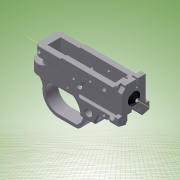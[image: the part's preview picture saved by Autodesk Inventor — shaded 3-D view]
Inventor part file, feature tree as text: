
AUTODESK INVENTOR PART (.ipt)
format: ipt  version: 2011 (Build 150239000, 239)  size: 1,561,600 bytes
history: native  units: in
note: dims shown in document units (in); Inventor stores cm internally (conversion verified against a paired STEP export)
features: sketch x72, extrude x66, fillet x50, projected_geometry x7, hole x5, reference x5, other x1, plane x1, revolve x1
ambient origin geometry x8: Origin, YZ Plane, XZ Plane, XY Plane, X Axis, Y Axis, Z Axis, Center Point
bodies: Solid1 (feature_tree)
feature tree (208):
  extrude  "Extrusion1"  Depth=3.698in
  hole  "Hole1"  [1 undecoded]
  extrude  "Extrusion2"  Depth=0.235in
  sketch  "Sketch4"  dims[d16=0.235in d17=0.235in]
  extrude  "Extrusion3"  Depth=2.655in
  extrude  "Extrusion4"  Depth=0.778in
  extrude  "Extrusion5"  Depth=1.0in TaperAngle=0.0deg
  extrude  "Extrusion6"  Depth=1.244in TaperAngle=0.0deg
  extrude  "Extrusion7"  Depth=0.4805in
  extrude  "Extrusion8"  Depth=0.821in
  extrude  "Extrusion9"  Depth=1.244in TaperAngle=0.0deg
  extrude  "Extrusion10"  Depth=0.44in
  extrude  "Extrusion11"  Depth=0.174in
  extrude  "Extrusion12"  Depth=0.105in TaperAngle=0.0deg
  fillet  "Fillet2"  Radius=0.105in
  fillet  "Fillet3"  Radius=0.442in
  extrude  "Extrusion13"  Depth=0.092in TaperAngle=0.0deg
  extrude  "Extrusion14"  Depth=0.125in
  other  "Work Axis1"
  plane  "Work Plane1"
  revolve  "Revolution1"  [1 undecoded]
  extrude  "Extrusion15"  Depth=0.131in TaperAngle=0.0deg
  extrude  "Extrusion16"  TaperAngle=90.0deg  [1 undecoded]
  extrude  "Extrusion17"  Depth=0.1875in TaperAngle=0.0deg
  extrude  "Extrusion19"  Depth=0.44in
  extrude  "Extrusion20"  Depth=0.4805in
  extrude  "Extrusion21"  Depth=0.46in TaperAngle=0.0deg
  fillet  "Fillet4"  Radius=0.46in
  fillet  "Fillet5"  Radius=0.895in
  fillet  "Fillet6"  Radius=0.2375in
  fillet  "Fillet7"  Radius=0.46in
  fillet  "Fillet8"  Radius=0.0625in
  fillet  "Fillet9"  Radius=0.0625in
  fillet  "Fillet10"  Radius=0.0625in
  extrude  "Extrusion22"  Depth=0.0625in
  fillet  "Fillet11"  Radius=0.0625in
  fillet  "Fillet12"  Radius=0.0625in
  extrude  "Extrusion23"  Depth=0.0625in
  extrude  "Extrusion24"  Depth=0.46in TaperAngle=0.0deg
  fillet  "Fillet13"  Radius=1.125in
  extrude  "Extrusion25"  Depth=0.042in
  extrude  "Extrusion26"  Depth=0.042in TaperAngle=0.0deg
  fillet  "Fillet15"  Radius=0.042in
  extrude  "Extrusion27"  Depth=0.085in TaperAngle=0.0deg
  extrude  "Extrusion28"  Depth=0.085in TaperAngle=0.0deg
  extrude  "Extrusion29"  Depth=0.375in
  extrude  "Extrusion30"  Depth=0.1875in
  fillet  "Fillet16"  Radius=0.125in
  fillet  "Fillet17"  Radius=0.125in
  fillet  "Fillet18"  Radius=0.0312in
  fillet  "Fillet19"  Radius=0.0312in
  fillet  "Fillet20"  Radius=0.0312in
  fillet  "Fillet21"  Radius=0.0312in
  fillet  "Fillet22"  Radius=0.0312in
  fillet  "Fillet23"  Radius=0.0312in
  fillet  "Fillet24"  Radius=0.0312in
  fillet  "Fillet25"  Radius=0.0312in
  fillet  "Fillet26"  Radius=0.085in
  fillet  "Fillet27"  Radius=0.911in
  fillet  "Fillet28"  Radius=1.781in
  extrude  "Extrusion31"  Depth=0.6in
  extrude  "Extrusion32"  Depth=0.583in
  extrude  "Extrusion33"  Depth=0.125in
  extrude  "Extrusion34"  Depth=0.085in TaperAngle=0.0deg
  extrude  "Extrusion35"  Depth=0.125in TaperAngle=0.0deg
  fillet  "Fillet29"  Radius=0.0625in
  fillet  "Fillet30"  Radius=0.0625in
  fillet  "Fillet31"  Radius=0.0625in
  fillet  "Fillet32"  Radius=0.0625in
  fillet  "Fillet33"  Radius=0.0625in
  extrude  "Extrusion36"  Depth=1.471in
  hole  "Hole2"  [1 undecoded]
  extrude  "Extrusion37"  Depth=1.975in
  extrude  "Extrusion38"  Depth=0.3205in
  hole  "Hole3"  [1 undecoded]
  extrude  "Extrusion39"  Depth=1.977in
  extrude  "Extrusion40"  Depth=0.5in
  extrude  "Extrusion41"  Depth=0.266in
  fillet  "Fillet34"  Radius=1.125in
  fillet  "Fillet35"  Radius=1.765in
  extrude  "Extrusion42"  Depth=0.1875in
  fillet  "Fillet36"  Radius=1.25in
  extrude  "Extrusion43"  Depth=0.0625in
  extrude  "Extrusion44"  Depth=0.25in TaperAngle=0.0deg
  fillet  "Fillet37"  Radius=0.125in
  fillet  "Fillet38"  Radius=0.184in
  fillet  "Fillet39"  Radius=0.184in
  fillet  "Fillet40"  Radius=0.125in
  fillet  "Fillet41"  Radius=0.0312in
  fillet  "Fillet42"  Radius=0.0312in
  extrude  "Extrusion45"  Depth=0.0312in
  hole  "Hole4"  [1 undecoded]
  extrude  "Extrusion46"  Depth=0.326in
  extrude  "Extrusion47"  Depth=0.6in TaperAngle=0.0deg
  fillet  "Fillet43"  Radius=0.911in
  fillet  "Fillet44"  Radius=0.75in
  extrude  "Extrusion48"  Depth=0.6in TaperAngle=0.0deg
  extrude  "Extrusion49"  Depth=0.0312in
  extrude  "Extrusion50"  Depth=1.0in TaperAngle=0.0deg
  extrude  "Extrusion51"  Depth=1.0in TaperAngle=0.0deg
  fillet  "Fillet45"  Radius=0.1125in
  fillet  "Fillet46"  Radius=0.125in
  extrude  "Extrusion52"  Depth=0.1125in TaperAngle=0.0deg
  extrude  "Extrusion53"  Depth=0.1125in TaperAngle=0.0deg
  extrude  "Extrusion54"  Depth=0.1125in TaperAngle=0.0deg
  fillet  "Fillet47"  Radius=2.321in
  extrude  "Extrusion55"  Depth=1.721in
  hole  "Hole5"  [1 undecoded]
  extrude  "Extrusion56"  Depth=1.5in TaperAngle=0.0deg
  extrude  "Extrusion57"  Depth=1.5in TaperAngle=0.0deg
  extrude  "Extrusion58"  Depth=0.125in
  extrude  "Extrusion59"  Depth=1.5in TaperAngle=0.0deg
  extrude  "Extrusion60"  Depth=1.5in TaperAngle=0.0deg
  fillet  "Fillet48"  Radius=0.125in
  fillet  "Fillet49"  Radius=1.5in
  fillet  "Fillet50"  Radius=0.125in
  extrude  "Extrusion61"  Depth=1.5in TaperAngle=0.0deg
  extrude  "Extrusion62"  [1 undecoded]
  extrude  "Extrusion63"  [1 undecoded]
  fillet  "Fillet51"  [1 undecoded]
  extrude  "Extrusion64"  [1 undecoded]
  fillet  "Fillet52"  [1 undecoded]
  extrude  "Extrusion65"  [1 undecoded]
  extrude  "Extrusion66"  [1 undecoded]
  extrude  "Extrusion67"  [1 undecoded]
  sketch  "Sketch1"  dims[d0=1.0in d1=3.698in]
  sketch  "Sketch2"  dims[d2=0.97in d3=0.0in]
  sketch  "Sketch3"  dims[d5=0.1875in d6=0.5in d7=0.375in d8=0.25in d9=0.5635in d10=0.75in d11=0.8108in d12=0.198in d13=0.0in]
  sketch  "Sketch5"  dims[d18=0.65in d19=2.655in]
  sketch  "Sketch6"  dims[d20=3.596in d21=0.778in]
  sketch  "Sketch7"  dims[d22=3.886in d23=1.0in d24=0.0in]
  sketch  "Sketch8"  dims[d25=1.0in d26=0.0in d27=1.244in d28=0.0in]
  sketch  "Sketch9"  dims[d29=0.961in d30=0.4805in]
  sketch  "Sketch10"  dims[d31=0.821in d32=0.821in]
  sketch  "Sketch11"  dims[d33=1.244in d34=0.0in d35=1.244in d36=0.0in]
  sketch  "Sketch12"  dims[d37=1.244in d38=0.0in d39=0.44in]
  sketch  "Sketch13"  dims[d40=0.585in d41=0.174in]
  sketch  "Sketch14"  dims[d42=0.125in d43=0.105in d44=0.0in d45=0.105in d46=0.0in d47=0.442in]
  sketch  "Sketch15"  dims[d48=0.092in d49=0.0in d50=0.092in d51=0.0in]
  sketch  "Sketch16"  dims[d52=0.125in d53=0.125in]
  projected_geometry  "Projected Loop2"
  sketch  "Sketch17"  dims[d67=0.458in d68=0.0in d69=0.48in]
  sketch  "Sketch18"  dims[d70=0.148in d71=0.131in d72=0.0in]
  sketch  "Sketch19"  dims[d73=90.0deg d74=90.0deg]
  sketch  "Sketch21"  dims[d75=0.418in d76=0.1875in d77=0.0in]
  projected_geometry  "Projected Loop3"
  sketch  "Sketch22"  dims[d80=0.1875in d81=0.0in d82=0.44in]
  sketch  "Sketch23"  dims[d83=0.4805in d84=0.4805in]
  sketch  "Sketch24"  dims[d87=0.55in d88=0.0in d91=0.46in d92=0.0in d93=0.46in d94=0.0in d95=0.895in d96=0.2375in d97=0.2375in d98=0.46in d99=0.0in d100=0.0625in d101=0.0625in d102=0.0625in]
  sketch  "Sketch25"  dims[d103=0.0625in d104=0.0625in d105=0.0625in d106=0.0625in]
  sketch  "Sketch26"  dims[d107=0.46in d108=0.0in d109=0.0625in]
  sketch  "Sketch27"  dims[d110=0.0625in d111=0.46in d112=0.0in d113=1.125in]
  sketch  "Sketch28"  dims[d114=0.042in d115=0.0in d116=0.042in]
  sketch  "Sketch29"  dims[d118=1.769in d119=0.042in d120=0.0in d121=0.042in d122=0.0in]
  sketch  "Sketch30"  dims[d123=0.375in d124=0.085in d125=0.0in]
  sketch  "Sketch31"  dims[d126=0.085in d127=0.0in d128=0.085in d129=0.0in]
  sketch  "Sketch32"  dims[d130=0.085in d131=0.0in d132=0.375in]
  sketch  "Sketch33"  dims[d133=0.125in d134=0.1875in d135=0.125in d136=0.125in d137=0.0312in d138=0.0312in d139=0.0312in d140=0.0312in d141=0.0312in d142=0.0312in d143=0.0312in d144=0.0312in d147=0.085in d148=0.0in d149=0.911in d150=1.781in]
  sketch  "Sketch34"  dims[d152=0.085in d153=0.6in]
  sketch  "Sketch35"  dims[d156=1.1875in d157=0.583in]
  sketch  "Sketch36"  dims[d158=0.085in d159=0.0in d168=0.125in]
  sketch  "Sketch37"  dims[d174=0.125in d175=0.085in d176=0.0in]
  sketch  "Sketch38"  dims[d177=0.125in d178=0.0in d179=0.125in d180=0.0in d181=0.0625in d182=0.0625in d183=0.0625in d184=0.0625in d185=0.0625in]
  sketch  "Sketch39"  dims[d186=1.471in d187=1.471in]
  sketch  "Sketch40"  dims[d188=0.3125in d189=0.125in d190=0.0in]
  sketch  "Sketch41"  dims[d191=1.304in]
  projected_geometry  "Projected Loop4"
  sketch  "Sketch42"  dims[d192=0.125in d193=0.5in d194=0.375in d195=0.25in d196=0.5635in d197=0.75in d198=0.8108in d199=1.975in]
  sketch  "Sketch43"  dims[d200=0.3205in d201=0.3205in]
  projected_geometry  "Projected Loop5"
  sketch  "Sketch44"  dims[d202=0.597in d203=0.125in d204=0.0in]
  sketch  "Sketch45"  dims[d205=0.125in d206=0.0in d207=1.977in]
  sketch  "Sketch46"  dims[d208=0.475in]
  sketch  "Sketch47"  dims[d209=0.125in d210=0.5in d211=0.375in d212=0.25in d213=0.5635in d214=0.75in d215=0.8108in d216=0.5in]
  sketch  "Sketch48"  dims[d217=0.532in d218=0.266in d219=0.266in d220=0.304in d221=1.125in d222=0.0in d224=1.765in]
  sketch  "Sketch49"  dims[d225=0.911in d226=0.1875in d227=0.1875in d228=1.25in d229=0.0in]
  sketch  "Sketch50"  dims[d230=0.25in d231=0.0in d232=0.0625in]
  sketch  "Sketch51"  dims[d233=0.0625in d234=0.25in d235=0.0in d236=0.125in d240=0.184in d241=0.0in d242=0.184in d243=0.0in d244=0.125in d245=0.0312in d246=0.0312in]
  sketch  "Sketch52"  dims[d247=0.0312in d248=0.0312in]
  projected_geometry  "Projected Loop6"
  sketch  "Sketch53"  dims[d249=0.0312in d250=0.318in]
  sketch  "Sketch54"  dims[d252=0.063in d253=0.326in]
  sketch  "Sketch55"  dims[d255=0.326in d256=0.6in d257=0.0in d259=0.911in d260=0.75in]
  sketch  "Sketch56"  dims[d261=0.125in d262=0.5in d263=0.375in d264=0.25in d265=0.5635in d266=0.75in d267=0.8108in d270=0.6in d271=0.0in]
  sketch  "Sketch57"  dims[d272=0.6in d273=0.0in d274=0.0312in]
  projected_geometry  "Projected Loop7"
  sketch  "Sketch58"  dims[d275=0.0312in d276=1.0in d277=0.0in]
  sketch  "Sketch59"  dims[d278=0.1125in d279=0.0in d280=1.0in d281=0.0in d282=0.1125in d283=0.0in d284=0.125in]
  sketch  "Sketch60"  dims[d285=0.125in d286=0.1125in d287=0.0in]
  sketch  "Sketch61"  dims[d288=0.1125in d289=0.0in d290=0.1125in d291=0.0in]
  sketch  "Sketch62"  dims[d292=0.0312in d293=0.1125in d294=0.0in d295=2.321in]
  sketch  "Sketch63"  dims[d296=1.02in]
  sketch  "Sketch64"  dims[d297=0.096in d298=0.5in d299=0.375in d300=0.25in d301=0.5635in d302=0.75in d303=0.8108in d304=1.721in]
  reference  "Reference5"
  reference  "Reference6"
  reference  "Reference7"
  reference  "Reference8"
  reference  "Reference9"
  sketch  "Sketch65"  dims[d305=0.25in d306=0.1125in d307=0.0in]
  sketch  "Sketch66"  dims[d308=0.1125in d309=0.0in d310=1.5in d311=0.0in]
  sketch  "Sketch67"  dims[d312=1.5in d313=0.0in d314=1.5in d315=0.0in]
  projected_geometry  "Projected Loop8"
  sketch  "Sketch68"  dims[d316=0.125in d317=0.125in]
  sketch  "Sketch69"  dims[d318=0.125in d319=1.5in d320=0.0in]
  sketch  "Sketch70"  dims[d321=1.5in d322=0.0in d323=1.5in d324=0.0in d325=0.125in d326=1.5in d327=0.0in d328=0.125in]
  sketch  "Sketch71"  dims[d330=1.5in d331=0.0in d332=1.5in d333=0.0in]
  sketch  "Sketch72"  dims[d334=0.5in d335=0.0in]
  sketch  "Sketch73"
note: 15 required parameter values undecoded (feature->parameter linkage not recoverable at this tier; creation-order binding heuristic only, values carry confidence <= 0.55)